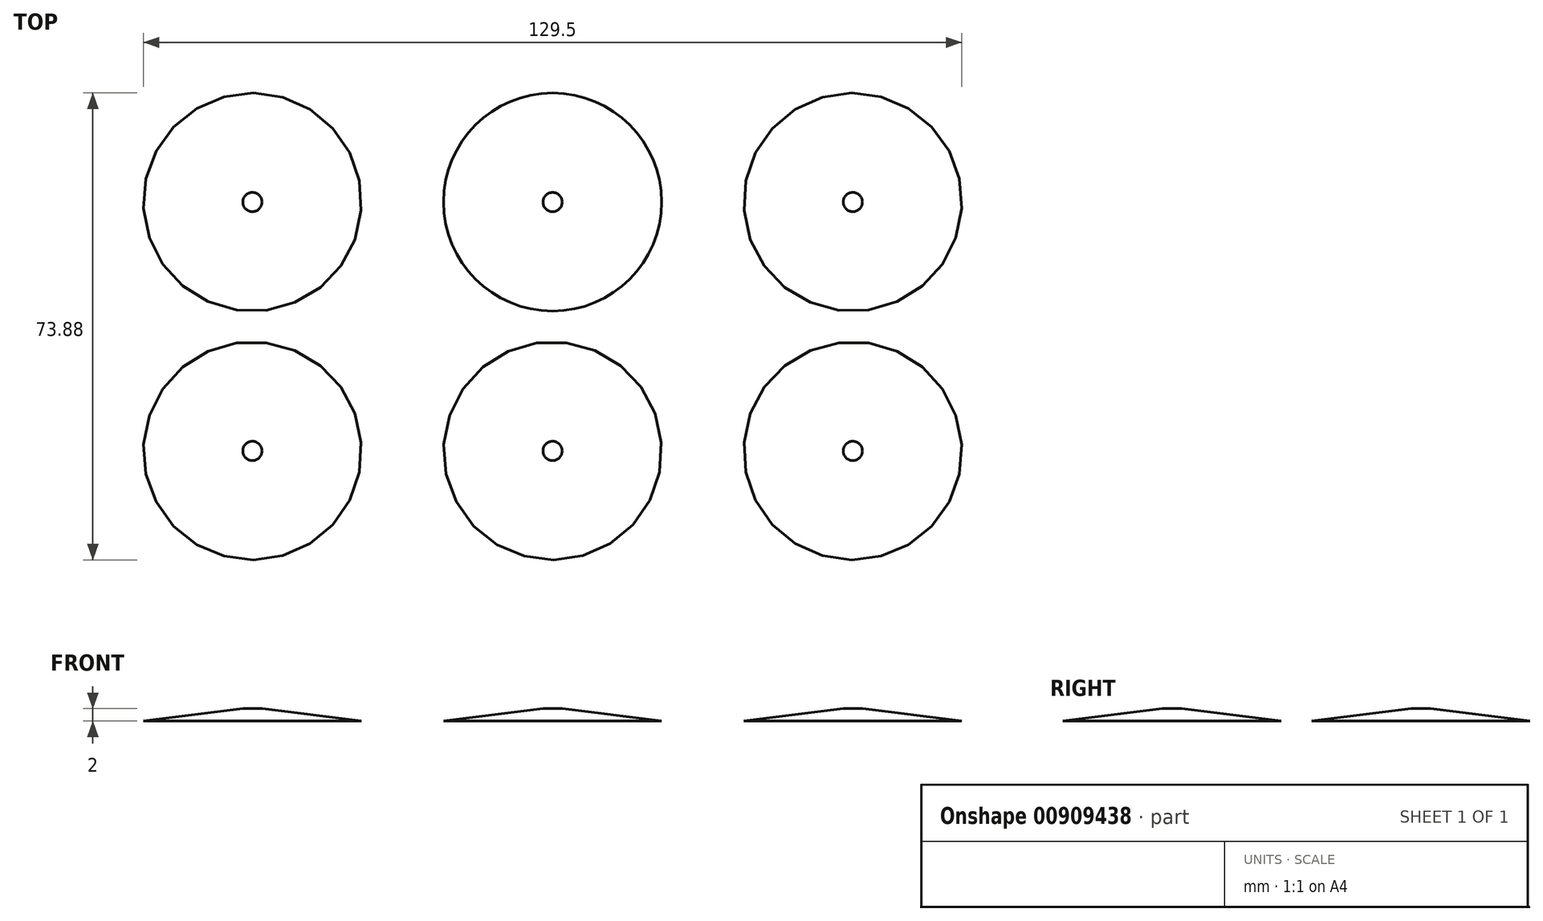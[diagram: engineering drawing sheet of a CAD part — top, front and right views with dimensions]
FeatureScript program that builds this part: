
annotation { "Feature Type Name" : "Feature", "Feature Type Description" : "" }
export const myFeature = defineFeature(function(context is Context, id is Id, definition is map)
    precondition{}
    {
        {
            var Q0;
            Q0=qCreatedBy(makeId("Top.planeOp"),FACE);
            var sketch = newSketch(context, id + "F0", { "sketchPlane" : qUnion([Q0])});
            skLineSegment(sketch, "E0.bottom", {"start": v(71.12, -39.37) * mm, "end": v(-71.12, -39.37) * mm});
            skLineSegment(sketch, "E0.top", {"start": v(71.12, 39.37) * mm, "end": v(-71.12, 39.37) * mm});
            skLineSegment(sketch, "E0.left", {"start": v(71.12, -39.37) * mm, "end": v(71.12, 39.37) * mm});
            skLineSegment(sketch, "E0.right", {"start": v(-71.12, -39.37) * mm, "end": v(-71.12, 39.37) * mm});
            skPoint(sketch, "E0.middle", {"position": v(0, 0) * mm});
            skSolve(sketch);
        }
        {
            var Q0;
            Q0=makeQuery(id+"F0.imprint","IMPRINT",FACE,{"disambiguationData":[TD([[makeQuery(id+"F0.imprint","IMPRINT",EDGE,{"derivedFrom":sQuery(id+"F0.wireOp",EDGE,"E0.bottom")}),-1.0]])]});
            var sketch = newSketch(context, id + "F1", { "sketchPlane" : qUnion([Q0])});
            skLineSegment(sketch, "E1", {"start": v(-71.24, 19.69) * mm, "end": v(71, 19.69) * mm});
            skSolve(sketch);
        }
        {
            var Q0;
            Q0=makeQuery(id+"F0.imprint","IMPRINT",FACE,{"disambiguationData":[TD([[makeQuery(id+"F0.imprint","IMPRINT",EDGE,{"derivedFrom":sQuery(id+"F0.wireOp",EDGE,"E0.bottom")}),-1.0]])]});
            var sketch = newSketch(context, id + "F2", { "sketchPlane" : qUnion([Q0])});
            skCircle(sketch, "E2", {"center": v(0, 19.69) * mm, "radius": 17.25 * mm});
            skSolve(sketch);
        }
        {
            assignVariable(context, id + "F3", {"name" : "coneheight", "anyValue" : 2});
        }
        {
            var Q0;
            Q0=makeQuery(id+"F0.imprint","IMPRINT",FACE,{"disambiguationData":[TD([[makeQuery(id+"F0.imprint","IMPRINT",EDGE,{"derivedFrom":sQuery(id+"F0.wireOp",EDGE,"E0.bottom")}),-1.0]])]});
            cPlane(context, id + "F4", {"entities" : qUnion([Q0]), "cplaneType" : CPlaneType.OFFSET, "offset" : (getVariable(context, 'coneheight')) * mm, "width" : 152.4 * mm, "height" : 152.4 * mm});
        }
        {
            var Q0;
            Q0=qCreatedBy(id+"F4.planeOp",FACE);
            var sketch = newSketch(context, id + "F5", { "sketchPlane" : qUnion([Q0])});
            skCircle(sketch, "E3", {"center": v(0, 19.68) * mm, "radius": 1.52 * mm});
            skSolve(sketch);
        }
        {
            var Q0;
            Q0=makeQuery(id+"F2.imprint","IMPRINT",FACE,{"disambiguationData":[TD([[makeQuery(id+"F2.imprint","IMPRINT",EDGE,{"derivedFrom":sQuery(id+"F2.wireOp",EDGE,"E2")}),1.0]])]});
            var Q1;
            Q1=makeQuery(id+"F5.imprint","IMPRINT",FACE,{"disambiguationData":[TD([[makeQuery(id+"F5.imprint","IMPRINT",EDGE,{"derivedFrom":sQuery(id+"F5.wireOp",EDGE,"E3")}),1.0]])]});
            loft(context, id + "F6", {"sheetProfilesArray" : [{ "sheetProfileEntities" : qUnion([Q0]) }, { "sheetProfileEntities" : qUnion([Q1]) }]});
        }
        {
            var Q0;
            Q0=makeQuery(id+"F6.opLoft","SWEPT_BODY",BODY,{"disambiguationData":[OSD([makeQuery(id+"F2.imprint","IMPRINT",FACE,{"disambiguationData":[TD([[makeQuery(id+"F2.imprint","IMPRINT",EDGE,{"derivedFrom":sQuery(id+"F2.wireOp",EDGE,"E2")}),1.0]])]}),makeQuery(id+"F5.imprint","IMPRINT",FACE,{"disambiguationData":[TD([[makeQuery(id+"F5.imprint","IMPRINT",EDGE,{"derivedFrom":sQuery(id+"F5.wireOp",EDGE,"E3")}),1.0]])]})])]});
            var Q1;
            Q1=qCreatedBy(makeId("Front.planeOp"),FACE);
            mirror(context, id + "F7", {"entities" : qUnion([Q0]), "mirrorPlane" : qUnion([Q1])});
        }
        {
            var Q0;
            Q0=qCreatedBy(makeId("Right.planeOp"),FACE);
            cPlane(context, id + "F8", {"entities" : qUnion([Q0]), "cplaneType" : CPlaneType.OFFSET, "offset" : 23.75 * mm, "width" : 152.4 * mm, "height" : 152.4 * mm});
        }
        {
            var Q0;
            Q0=makeQuery(id+"F6.opLoft","SWEPT_BODY",BODY,{"disambiguationData":[OSD([makeQuery(id+"F2.imprint","IMPRINT",FACE,{"disambiguationData":[TD([[makeQuery(id+"F2.imprint","IMPRINT",EDGE,{"derivedFrom":sQuery(id+"F2.wireOp",EDGE,"E2")}),1.0]])]}),makeQuery(id+"F5.imprint","IMPRINT",FACE,{"disambiguationData":[TD([[makeQuery(id+"F5.imprint","IMPRINT",EDGE,{"derivedFrom":sQuery(id+"F5.wireOp",EDGE,"E3")}),1.0]])]})])]});
            var Q1;
            Q1=makeQuery(id+"F7.opPattern","COPY",BODY,{"derivedFrom":makeQuery(id+"F6.opLoft","SWEPT_BODY",BODY,{"disambiguationData":[OSD([makeQuery(id+"F2.imprint","IMPRINT",FACE,{"disambiguationData":[TD([[makeQuery(id+"F2.imprint","IMPRINT",EDGE,{"derivedFrom":sQuery(id+"F2.wireOp",EDGE,"E2")}),1.0]])]}),makeQuery(id+"F5.imprint","IMPRINT",FACE,{"disambiguationData":[TD([[makeQuery(id+"F5.imprint","IMPRINT",EDGE,{"derivedFrom":sQuery(id+"F5.wireOp",EDGE,"E3")}),1.0]])]})])]}),"instanceName":"1"});
            var Q2;
            Q2=qCreatedBy(id+"F8.planeOp",FACE);
            mirror(context, id + "F9", {"entities" : qUnion([Q0, Q1]), "mirrorPlane" : qUnion([Q2])});
        }
        {
            var Q0;
            Q0=makeQuery(id+"F9.opPattern","COPY",BODY,{"derivedFrom":makeQuery(id+"F6.opLoft","SWEPT_BODY",BODY,{"disambiguationData":[OSD([makeQuery(id+"F2.imprint","IMPRINT",FACE,{"disambiguationData":[TD([[makeQuery(id+"F2.imprint","IMPRINT",EDGE,{"derivedFrom":sQuery(id+"F2.wireOp",EDGE,"E2")}),1.0]])]}),makeQuery(id+"F5.imprint","IMPRINT",FACE,{"disambiguationData":[TD([[makeQuery(id+"F5.imprint","IMPRINT",EDGE,{"derivedFrom":sQuery(id+"F5.wireOp",EDGE,"E3")}),1.0]])]})])]}),"instanceName":"1"});
            var Q1;
            Q1=makeQuery(id+"F9.opPattern","COPY",BODY,{"derivedFrom":makeQuery(id+"F7.opPattern","COPY",BODY,{"derivedFrom":makeQuery(id+"F6.opLoft","SWEPT_BODY",BODY,{"disambiguationData":[OSD([makeQuery(id+"F2.imprint","IMPRINT",FACE,{"disambiguationData":[TD([[makeQuery(id+"F2.imprint","IMPRINT",EDGE,{"derivedFrom":sQuery(id+"F2.wireOp",EDGE,"E2")}),1.0]])]}),makeQuery(id+"F5.imprint","IMPRINT",FACE,{"disambiguationData":[TD([[makeQuery(id+"F5.imprint","IMPRINT",EDGE,{"derivedFrom":sQuery(id+"F5.wireOp",EDGE,"E3")}),1.0]])]})])]}),"instanceName":"1"}),"instanceName":"1"});
            var Q2;
            Q2=qCreatedBy(makeId("Right.planeOp"),FACE);
            mirror(context, id + "F10", {"entities" : qUnion([Q0, Q1]), "mirrorPlane" : qUnion([Q2])});
        }
    });
